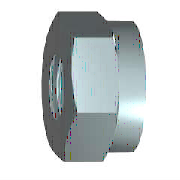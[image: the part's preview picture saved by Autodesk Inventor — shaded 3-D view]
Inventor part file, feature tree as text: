
AUTODESK INVENTOR PART (.ipt)
format: ipt  version: 2022 (Build 260153000, 153)  size: 179,712 bytes
history: native  units: mm (DEFAULTED — no unit token found)
features: sketch x4, extrude x1, chamfer x1, hole x1, other x1, plane x1
ambient origin geometry x7: Origin, YZ Plane, XZ Plane, X Axis, Y Axis, Z Axis, Center Point
bodies: Solid1 (feature_tree), Body (feature_tree)
feature tree (9):
  extrude  "Ring"  Depth=5.4mm
  chamfer  "Chamfer1"  Distance=8.88mm
  hole  "Thread"  [1 undecoded]
  other  "Work Axis1"
  plane  "Work Plane1"
  sketch  "Sketch1"  dims[d0=11.547005mm d1=5.4mm]
  sketch  "Sketch3"  dims[d3=30.0deg]
  sketch  "Sketch2"  dims[d2=0.0mm]
  sketch  "Sketch4"  dims[d4=30.0deg d5=8.88mm d6=8.88mm d26=90.0deg d7=8.88mm d8=3.1mm d9=0.0mm d30=4.917mm d31=6.0mm d32=4.0mm d33=2.0mm d34=14.3117mm d35=8.0mm d36=20.594885mm d10=0.541266mm d11=30.0deg d12=0.541266mm d13=30.0deg d14=0.0mm d15=0.0mm d45=0.0mm d46=0.541266mm d47=0.541266mm d48=0.0mm]
note: 1 required parameter value undecoded (feature->parameter linkage not recoverable at this tier; creation-order binding heuristic only, values carry confidence <= 0.55)
